# Revit family: 55162131(2022)
name_source: partatom
category: Plumbing Fixtures
revit_build: Autodesk Revit 2018 (Build: 20170223_1515(x64)
units: mm (PartAtom-declared; Revit-internal decimal feet)

## family parameters
Always vertical = Yes
Cut with Voids When Loaded = No
OmniClass Number = 23.45.55.00
OmniClass Title = Sanitary Faucets, Wastes
Part Type = Normal
Room Calculation Point = No
Round Connector Dimension = Use Diameter
Shared = No
Work Plane-Based = No

## types (1)
- 55162131 Bath and shower faucet with shower set
    2D/3D/BIM Files URL = http://static.hansa.com
    Additional Features = protected against back-flow in domestic use (according to DIN EN 1717)
    Aerator = Standard aerator
    AssetType = Fixed
    BIMObjectName = 55162131(2022)
    Backflow Prevention EN1717 = EB
    BodyMaterial = Brass
    Brand = HANSA
    Catalog Drawing URL = http://static.hansa.com
    CloseOffRating = 0
    Color = Chrome
    Connection = Eccentric coupling(s)
    Connection Size = G1/2
    Dimension Drawing URL = http://static.hansa.com
    Diverter = Turn operated diverter;Integrated into flow control handle
    DurationUnit = Year
    EAN Number = 4057304019180
    EN Standard = EN 1111
    ETIM Class Number = EC010862 Bath mixing tap
    Eco Flow At 300kPa = 0.2 L/s
    FDV Document URL = http://www.hansa.com
    FaucetMainMaterial = Brass
    FaucetNominalDepth = 175 mm
    FaucetNominalHeight = 79 mm
    FaucetNominalWidth = 290 mm  [stored 0.951444 ft]
    Features = Thermostatic
    Finish = Polished
    Flow Drawing URL = http://static.hansa.com
    Flow Rate At 300kPa = 0.3 L/s
    FlowCoefficient = 0
    Group = Bath and shower faucet
    HandShowerNominalDepth = 127 mm
    HandShowerNominalHeight = 700 mm
    HandShowerNominalWidth = 142 mm  [stored 0.465879 ft]
    IfcExportAs = IfcValveType
    IfcExportType = FAUCET
    Installation Type = Wall mounted
    Installation Width = cc150 ± 15 mm
    Installation and Maintenance Guide URL = http://static.hansa.com
    Lever Handle = Temperature control handle;Flow control handle
    Manufacturer = HANSA
    ManufacturerName = HANSA
    ManufacturerURL = http://www.hansa.com
    Market = International;Germany
    Material = Brass
    Max. Hot Water Supply = 65 °C
    Mechanical Parts = Thermostatic cartridge for automatic temperature control;Litter filter(s);Ceramic head part for flow control
    Mobile Product Information URL = http://mpi.hansa.com
    Model = 55162131 Bath and shower faucet with shower set
    ModelReference = 55162131
    NBSDescription = Water supply fittings for baths
    NBSReference = 45-35-70/315
    Name = 55162131 Bath and shower faucet with shower set
    Name_en = 55162131 Bath and shower faucet with shower set
    Noise Class = II (ISO 3822)
    Product Code = 55162131
    Product Family = 5160
    Product Image URL = http://static.hansa.com
    Product URL = http://static.hansa.com
    Sales Package dimensions (LxWxH) = 715 x 210 x 85
    Shape = Sculptured
    Shower Parts = Hand shower;Shower rail;Shower hose (1500 mm);Eco flow control
    Shower Spray Number = 3 shower sprays
    Size = Faucet: 290x180x80 mm; Shower: 140x130x700 mm
    Spout Projection = 160 mm
    Spout Type = Fixed spout
    Surface treatment = Chrome
    Technical DataSheet URL = http://www.hansa.com
    Temperature = Thermostatic temperature control
    Temperature Adjustments = The housing of the fittings conducts minimal heat;Safety stop against scalding at 38°C
    UNSPSC Class Number = 30181700 Faucets or taps
    URL Declaration of Conformity = http://static.hansa.com
    URL REACH = http://static.hansa.com
    URL UWL = http://static.hansa.com
    Uniclass2 = Pr_40_30_96_07
    Uniclass2015Description = Bath manual water supply sets
    Uniclass2015Reference = Pr_40_20_87_07
    Version = 1
    VersionDate = 23/11/2022
    Warranty Information URL = http://warranty.hansa.com
    WarrantyDescription = http://warranty.hansa.com
    WarrantyDurationUnit = Year
    Working Pressure = 100 - 1000 kPa

note: [stored X ft] marks values corroborated as IEEE doubles in the binary element streams (Revit-internal decimal feet)

## geometry (parser evidence)
native form markers: Sweep x9
no freeform markers — native parametric forms only
